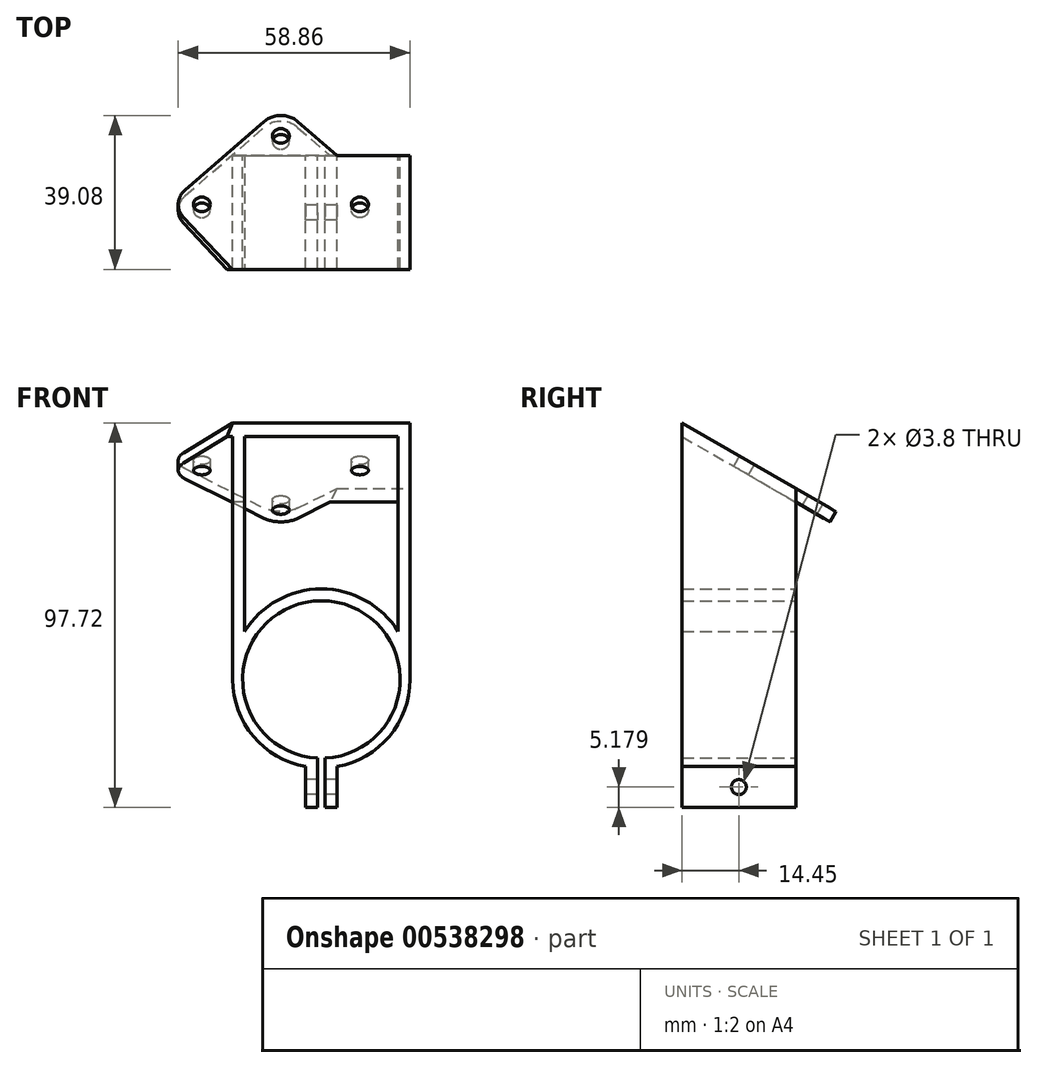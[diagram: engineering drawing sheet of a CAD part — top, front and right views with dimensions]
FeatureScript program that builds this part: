
annotation { "Feature Type Name" : "Feature", "Feature Type Description" : "" }
export const myFeature = defineFeature(function(context is Context, id is Id, definition is map)
    precondition{}
    {
        {
            var Q0;
            Q0=qCreatedBy(makeId("Front.planeOp"),FACE);
            var sketch = newSketch(context, id + "F0", { "sketchPlane" : qUnion([Q0])});
            skCircle(sketch, "E0", {"center": v(0, 0) * mm, "radius": 22.5 * mm});
            skLineSegment(sketch, "E1", {"start": v(-22.5, 0) * mm, "end": v(-22.5, 65.22) * mm});
            skLineSegment(sketch, "E2", {"start": v(22.5, 0) * mm, "end": v(22.5, 65.22) * mm});
            skLineSegment(sketch, "E3", {"start": v(22.5, 65.22) * mm, "end": v(-22.5, 65.22) * mm});
            skPoint(sketch, "E4", {"position": v(0, -22.5) * mm});
            skSolve(sketch);
        }
        {
            var Q0;
            Q0=makeQuery(id+"F0.imprint","IMPRINT",FACE,{"disambiguationData":[TD([[makeQuery(id+"F0.imprint","IMPRINT",EDGE,{"derivedFrom":sQuery(id+"F0.wireOp",EDGE,"E0")}),1.0]])]});
            var Q1;
            {var subQ0=sQuery(id+"F0.wireOp",EDGE,"E1");Q1=makeQuery(id+"F0.imprint","IMPRINT",FACE,{"disambiguationData":[TD([[makeQuery(id+"F0.imprint","IMPRINT",EDGE,{"derivedFrom":subQ0}),-1.0]])]});}
            extrude(context, id + "F1", {"entities" : qUnion([Q0, Q1]), "depth" : 28.9 * mm, "offsetDistance" : 25 * mm});
        }
        {
            var Q0;
            Q0=sQuery(id+"F0.wireOp",VERTEX,"E0.center");
            var Q1;
            Q1=makeQuery(id+"F1.opExtrude","SWEPT_BODY",BODY,{"disambiguationData":[OSD([sQuery(id+"F0.wireOp",EDGE,"E0")])]});
            hole(context, id + "F2", {"style" : HoleStyle.SIMPLE, "endStyle" : HoleEndStyle.THROUGH, "oppositeDirection" : true, "holeDiameter" : 40 * mm, "majorDiameter" : 5 * mm, "isTappedThrough" : true, "tappedDepth" : 12 * mm, "tapClearance" : 3, "locations" : qUnion([Q0]), "scope" : qUnion([Q1])});
        }
        {
            var Q0;
            Q0=makeQuery(id+"F1.opExtrude","SWEPT_FACE",FACE,{"disambiguationData":[OSD([sQuery(id+"F0.wireOp",EDGE,"E2")])]});
            var sketch = newSketch(context, id + "F3", { "sketchPlane" : qUnion([Q0])});
            skLineSegment(sketch, "E5", {"start": v(-28.9, 65.22) * mm, "end": v(0, 48.53) * mm});
            skSolve(sketch);
        }
        {
            var Q0;
            {var subQ0=sQuery(id+"F3.wireOp",EDGE,"E5");Q0=makeQuery(id+"F3.imprint","IMPRINT",FACE,{"disambiguationData":[TD([[makeQuery(id+"F3.imprint","IMPRINT",EDGE,{"derivedFrom":subQ0}),1.0]])]});}
            extrude(context, id + "F4", {"entities" : qUnion([Q0]), "operationType" : NewBodyOperationType.REMOVE, "endBound" : BoundingType.THROUGH_ALL, "oppositeDirection" : true, "depth" : 25 * mm, "offsetDistance" : 25 * mm});
        }
        {
            var Q0;
            {var subQ0=sQuery(id+"F0.wireOp",EDGE,"E0");var subQ1=makeQuery(id+"F0.imprint","INTERSECT",VERTEX,{"derivedFrom":[subQ0,sQuery(id+"F0.wireOp",EDGE,"E1")]});Q0=makeQuery(id+"F0.imprint","IMPRINT",FACE,{"disambiguationData":[TD([[makeQuery(id+"F0.imprint","IMPRINT",EDGE,{"disambiguationData":[TD([[subQ1,1.0]])],"derivedFrom":subQ0}),1.0]])]});}
            var sketch = newSketch(context, id + "F5", { "sketchPlane" : qUnion([Q0])});
            skLineSegment(sketch, "E6", {"start": v(0, -24.67) * mm, "end": v(0, 0) * mm, "construction": true});
            skLineSegment(sketch, "E7", {"start": v(1, 7.5) * mm, "end": v(1, 0.8) * mm});
            skLineSegment(sketch, "E8.MirrorCS", {"start": v(-1, 7.5) * mm, "end": v(-1, 0.8) * mm});
            skLineSegment(sketch, "E9.bottom", {"start": v(1, 0.8) * mm, "end": v(-1, 0.8) * mm});
            skLineSegment(sketch, "E9.top", {"start": v(1, -32.5) * mm, "end": v(-1, -32.5) * mm});
            skLineSegment(sketch, "E9.left", {"start": v(1, 0.8) * mm, "end": v(1, -32.5) * mm});
            skLineSegment(sketch, "E9.right", {"start": v(-1, 0.8) * mm, "end": v(-1, -32.5) * mm});
            skLineSegment(sketch, "E10.bottom", {"start": v(-1, 7.5) * mm, "end": v(-4, 7.5) * mm});
            skLineSegment(sketch, "E10.top", {"start": v(-1, -32.5) * mm, "end": v(-4, -32.5) * mm});
            skLineSegment(sketch, "E10.left", {"start": v(-1, 7.5) * mm, "end": v(-1, -32.5) * mm});
            skLineSegment(sketch, "E10.right", {"start": v(-4, 7.5) * mm, "end": v(-4, -32.5) * mm});
            skLineSegment(sketch, "E11.MirrorCS", {"start": v(4, 7.5) * mm, "end": v(4, -32.5) * mm});
            skLineSegment(sketch, "E12.MirrorCS", {"start": v(1, 7.5) * mm, "end": v(4, 7.5) * mm});
            skLineSegment(sketch, "E13.MirrorCS", {"start": v(1, -32.5) * mm, "end": v(4, -32.5) * mm});
            skSolve(sketch);
        }
        {
            var Q0;
            {var subQ0=sQuery(id+"F5.wireOp",EDGE,"E13.MirrorCS");Q0=makeQuery(id+"F5.imprint","IMPRINT",FACE,{"disambiguationData":[TD([[makeQuery(id+"F5.imprint","IMPRINT",EDGE,{"derivedFrom":subQ0}),1.0]])]});}
            var Q1;
            {var subQ0=sQuery(id+"F5.wireOp",EDGE,"E10.top");Q1=makeQuery(id+"F5.imprint","IMPRINT",FACE,{"disambiguationData":[TD([[makeQuery(id+"F5.imprint","IMPRINT",EDGE,{"derivedFrom":subQ0}),-1.0]])]});}
            extrude(context, id + "F6", {"entities" : qUnion([Q0, Q1]), "operationType" : NewBodyOperationType.ADD, "depth" : 28.9 * mm, "offsetDistance" : 25 * mm});
        }
        {
            var Q0;
            {var subQ0=sQuery(id+"F5.wireOp",EDGE,"E9.bottom");Q0=makeQuery(id+"F5.imprint","IMPRINT",FACE,{"disambiguationData":[TD([[makeQuery(id+"F5.imprint","IMPRINT",EDGE,{"derivedFrom":subQ0}),1.0]])]});}
            extrude(context, id + "F7", {"entities" : qUnion([Q0]), "operationType" : NewBodyOperationType.REMOVE, "endBound" : BoundingType.THROUGH_ALL, "depth" : 25 * mm, "offsetDistance" : 25 * mm});
        }
        {
            var Q0;
            Q0=makeQuery(id+"F6.opExtrude","SWEPT_FACE",FACE,{"disambiguationData":[OSD([sQuery(id+"F5.wireOp",EDGE,"E10.right")])]});
            var sketch = newSketch(context, id + "F8", { "sketchPlane" : qUnion([Q0])});
            skLineSegment(sketch, "E14", {"start": v(14.45, -22.14) * mm, "end": v(14.45, -32.5) * mm, "construction": true});
            skCircle(sketch, "E15", {"center": v(14.45, -27.32) * mm, "radius": 1.9 * mm});
            skSolve(sketch);
        }
        {
            var Q0;
            Q0=makeQuery(id+"F8.imprint","IMPRINT",FACE,{"disambiguationData":[TD([[makeQuery(id+"F8.imprint","IMPRINT",EDGE,{"derivedFrom":sQuery(id+"F8.wireOp",EDGE,"E15")}),1.0]])]});
            extrude(context, id + "F9", {"entities" : qUnion([Q0]), "operationType" : NewBodyOperationType.REMOVE, "endBound" : BoundingType.THROUGH_ALL, "oppositeDirection" : true, "depth" : 25 * mm, "offsetDistance" : 25 * mm});
        }
        {
            var Q0;
            {var subQ0=sQuery(id+"F0.wireOp",EDGE,"E0");Q0=makeQuery(id+"F6.boolean.opBoolean","MERGE",FACE,{"derivedFrom":[makeQuery(id+"F1.opExtrude","CAP_FACE",FACE,{"disambiguationData":[OSD([subQ0,sQuery(id+"F0.wireOp",EDGE,"E1"),sQuery(id+"F0.wireOp",EDGE,"E2"),sQuery(id+"F0.wireOp",EDGE,"E3")])],"isStart":false}),makeQuery(id+"F6.opExtrude","CAP_FACE",FACE,{"disambiguationData":[OSD([subQ0,sQuery(id+"F5.wireOp",EDGE,"E9.left"),sQuery(id+"F5.wireOp",EDGE,"E11.MirrorCS"),sQuery(id+"F5.wireOp",EDGE,"E13.MirrorCS")])],"isStart":false}),makeQuery(id+"F6.opExtrude","CAP_FACE",FACE,{"disambiguationData":[OSD([subQ0,sQuery(id+"F5.wireOp",EDGE,"E10.top"),sQuery(id+"F5.wireOp",EDGE,"E10.left"),sQuery(id+"F5.wireOp",EDGE,"E10.right")])],"isStart":false})]});}
            var Q1;
            {var subQ0=sQuery(id+"F0.wireOp",EDGE,"E0");Q1=makeQuery(id+"F6.boolean.opBoolean","MERGE",FACE,{"derivedFrom":[makeQuery(id+"F1.opExtrude","CAP_FACE",FACE,{"disambiguationData":[OSD([subQ0,sQuery(id+"F0.wireOp",EDGE,"E1"),sQuery(id+"F0.wireOp",EDGE,"E2"),sQuery(id+"F0.wireOp",EDGE,"E3")])],"isStart":true}),makeQuery(id+"F6.opExtrude","CAP_FACE",FACE,{"disambiguationData":[OSD([subQ0,sQuery(id+"F5.wireOp",EDGE,"E9.left"),sQuery(id+"F5.wireOp",EDGE,"E11.MirrorCS"),sQuery(id+"F5.wireOp",EDGE,"E13.MirrorCS")])],"isStart":true}),makeQuery(id+"F6.opExtrude","CAP_FACE",FACE,{"disambiguationData":[OSD([subQ0,sQuery(id+"F5.wireOp",EDGE,"E10.top"),sQuery(id+"F5.wireOp",EDGE,"E10.left"),sQuery(id+"F5.wireOp",EDGE,"E10.right")])],"isStart":true})]});}
            shell(context, id + "F10", {"entities" : qUnion([Q0, Q1]), "thickness" : 3 * mm});
        }
        {
            var Q0;
            Q0=makeQuery(id+"F4.boolean.opBoolean","COPY",FACE,{"derivedFrom":makeQuery(id+"F4.opExtrude","SWEPT_FACE",FACE,{"disambiguationData":[OSD([sQuery(id+"F3.wireOp",EDGE,"E5")])]})});
            var sketch = newSketch(context, id + "F11", { "sketchPlane" : qUnion([Q0])});
            skCircle(sketch, "E16", {"center": v(-30.36, -38.59) * mm, "radius": 2.15 * mm});
            skCircle(sketch, "E17", {"center": v(-10.28, -18.5) * mm, "radius": 2.15 * mm});
            skCircle(sketch, "E18", {"center": v(9.8, -38.59) * mm, "radius": 2.15 * mm});
            skPoint(sketch, "E19", {"position": v(22.5, -40.95) * mm});
            skLineSegment(sketch, "E20", {"start": v(-22.5, -57.64) * mm, "end": v(-35, -42.4) * mm});
            skLineSegment(sketch, "E21", {"start": v(-34.6, -34.34) * mm, "end": v(-14.52, -14.26) * mm});
            skLineSegment(sketch, "E22", {"start": v(-6.04, -14.26) * mm, "end": v(3.97, -24.27) * mm});
            skPoint(sketch, "E23.visualSharp", {"position": v(-38.44, -38.19) * mm});
            skArc(sketch, "E23.filletArc", {"start": v(-34.6, -34.34) * mm, "mid": v(-36.35, -38.3) * mm, "end": v(-35, -42.4) * mm});
            skPoint(sketch, "E24.visualSharp", {"position": v(-10.28, -10.02) * mm});
            skArc(sketch, "E24.filletArc", {"start": v(-6.04, -14.26) * mm, "mid": v(-10.28, -12.5) * mm, "end": v(-14.52, -14.26) * mm});
            skPoint(sketch, "E25", {"position": v(-22.5, -40.95) * mm});
            skSolve(sketch);
        }
        {
            var Q0;
            Q0=makeQuery(id+"F11.imprint","IMPRINT",FACE,{"disambiguationData":[TD([[makeQuery(id+"F11.imprint","IMPRINT",EDGE,{"derivedFrom":sQuery(id+"F11.wireOp",EDGE,"E16")}),-1.0]])]});
            extrude(context, id + "F12", {"entities" : qUnion([Q0]), "operationType" : NewBodyOperationType.ADD, "oppositeDirection" : true, "depth" : 3 * mm, "offsetDistance" : 25 * mm});
        }
        {
            var Q0;
            Q0=makeQuery(id+"F12.opExtrude","SWEPT_FACE",FACE,{"disambiguationData":[OSD([sQuery(id+"F0.wireOp",EDGE,"E1"),sQuery(id+"F3.wireOp",EDGE,"E5")])]});
            var Q1;
            Q1=makeQuery(id+"F1.opExtrude","SWEPT_FACE",FACE,{"disambiguationData":[OSD([sQuery(id+"F0.wireOp",EDGE,"E2")])]});
            extrude(context, id + "F13", {"entities" : qUnion([Q0]), "operationType" : NewBodyOperationType.REMOVE, "oppositeDirection" : true, "depth" : 25 * mm, "endBoundEntityFace" : qUnion([Q1]), "offsetDistance" : 25 * mm});
        }
        {
            var Q0;
            Q0=makeQuery(id+"F11.imprint","IMPRINT",FACE,{"disambiguationData":[TD([[makeQuery(id+"F11.imprint","IMPRINT",EDGE,{"derivedFrom":sQuery(id+"F11.wireOp",EDGE,"E18")}),1.0]])]});
            extrude(context, id + "F14", {"entities" : qUnion([Q0]), "operationType" : NewBodyOperationType.REMOVE, "oppositeDirection" : true, "depth" : 5 * mm, "offsetDistance" : 25 * mm});
        }
    });
